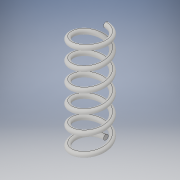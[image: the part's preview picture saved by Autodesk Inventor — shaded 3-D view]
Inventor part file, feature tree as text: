
AUTODESK INVENTOR PART (.ipt)
format: ipt  version: 2019 (Build 230136000, 136)  size: 474,624 bytes
history: native  units: in
note: dims shown in document units (in); Inventor stores cm internally (conversion verified against a paired STEP export)
features: helix x1, sketch x1
ambient origin geometry x8: Origin, YZ Plane, XZ Plane, XY Plane, X Axis, Y Axis, Z Axis, Center Point
bodies: Solid1 (feature_tree)
feature tree (2):
  helix  "Coil1"  [1 undecoded]
  sketch  "Sketch1"  dims[d1=0.0787in d2=1.7717in d3=0.3937in d4=1.5748in d5=1.9685in d6=0.0in d7=90.0deg d8=90.0deg d9=90.0deg d10=90.0deg]
note: 1 required parameter value undecoded (feature->parameter linkage not recoverable at this tier; creation-order binding heuristic only, values carry confidence <= 0.55)
